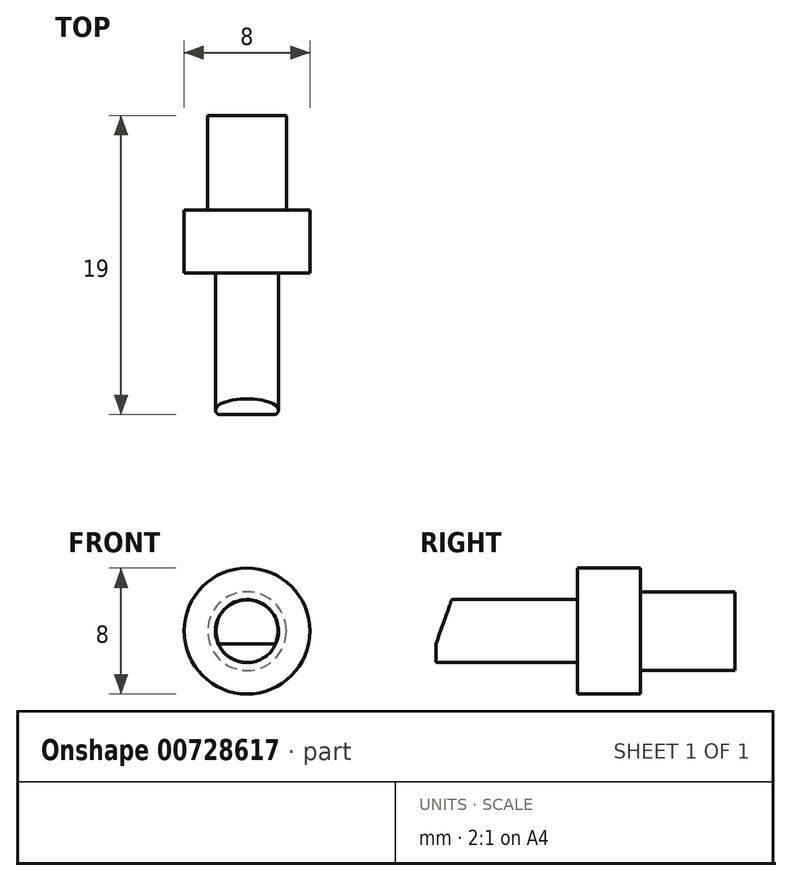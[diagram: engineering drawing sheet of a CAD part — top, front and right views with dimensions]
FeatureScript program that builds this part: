
annotation { "Feature Type Name" : "Feature", "Feature Type Description" : "" }
export const myFeature = defineFeature(function(context is Context, id is Id, definition is map)
    precondition{}
    {
        {
            var Q0;
            Q0=qCreatedBy(makeId("Front.planeOp"),FACE);
            var sketch = newSketch(context, id + "F0", { "sketchPlane" : qUnion([Q0])});
            skCircle(sketch, "E0", {"center": v(0, 0) * mm, "radius": 4 * mm});
            skSolve(sketch);
        }
        {
            var Q0;
            Q0=makeQuery(id+"F0.imprint","IMPRINT",FACE,{"disambiguationData":[TD([[makeQuery(id+"F0.imprint","IMPRINT",EDGE,{"derivedFrom":sQuery(id+"F0.wireOp",EDGE,"E0")}),1.0]])]});
            extrude(context, id + "F1", {"entities" : qUnion([Q0]), "oppositeDirection" : true, "depth" : 4 * mm, "offsetDistance" : 25 * mm});
        }
        {
            var Q0;
            Q0=makeQuery(id+"F1.opExtrude","CAP_FACE",FACE,{"disambiguationData":[OSD([sQuery(id+"F0.wireOp",EDGE,"E0")])],"isStart":true});
            var sketch = newSketch(context, id + "F2", { "sketchPlane" : qUnion([Q0])});
            skCircle(sketch, "E1", {"center": v(0, 0) * mm, "radius": 2 * mm});
            skSolve(sketch);
        }
        {
            var Q0;
            Q0=makeQuery(id+"F2.imprint","IMPRINT",FACE,{"disambiguationData":[TD([[makeQuery(id+"F2.imprint","IMPRINT",EDGE,{"derivedFrom":sQuery(id+"F2.wireOp",EDGE,"E1")}),1.0]])]});
            extrude(context, id + "F3", {"entities" : qUnion([Q0]), "operationType" : NewBodyOperationType.ADD, "depth" : 9 * mm, "offsetDistance" : 25 * mm});
        }
        {
            var Q0;
            Q0=makeQuery(id+"F1.opExtrude","CAP_FACE",FACE,{"disambiguationData":[OSD([sQuery(id+"F0.wireOp",EDGE,"E0")])],"isStart":false});
            var sketch = newSketch(context, id + "F4", { "sketchPlane" : qUnion([Q0])});
            skCircle(sketch, "E2", {"center": v(0, 0) * mm, "radius": 2.5 * mm});
            skSolve(sketch);
        }
        {
            var Q0;
            Q0=makeQuery(id+"F4.imprint","IMPRINT",FACE,{"disambiguationData":[TD([[makeQuery(id+"F4.imprint","IMPRINT",EDGE,{"derivedFrom":sQuery(id+"F4.wireOp",EDGE,"E2")}),1.0]])]});
            extrude(context, id + "F5", {"entities" : qUnion([Q0]), "operationType" : NewBodyOperationType.ADD, "depth" : 6 * mm, "offsetDistance" : 25 * mm});
        }
        {
            var Q0;
            Q0=qCreatedBy(makeId("Right.planeOp"),FACE);
            var sketch = newSketch(context, id + "F6", { "sketchPlane" : qUnion([Q0])});
            skLineSegment(sketch, "E3", {"start": v(-8, 2) * mm, "end": v(-9, 2) * mm});
            skLineSegment(sketch, "E4", {"start": v(-8, 2) * mm, "end": v(-9, -0.82) * mm});
            skLineSegment(sketch, "E5", {"start": v(-9, 2) * mm, "end": v(-9, -0.82) * mm});
            skSolve(sketch);
        }
        {
            var Q0;
            Q0 = qSketchRegion(id + "F6", true);
            extrude(context, id + "F7", {"entities" : qUnion([Q0]), "operationType" : NewBodyOperationType.REMOVE, "endBound" : BoundingType.SYMMETRIC, "oppositeDirection" : true, "depth" : 4 * mm, "offsetDistance" : 25 * mm});
        }
    });
